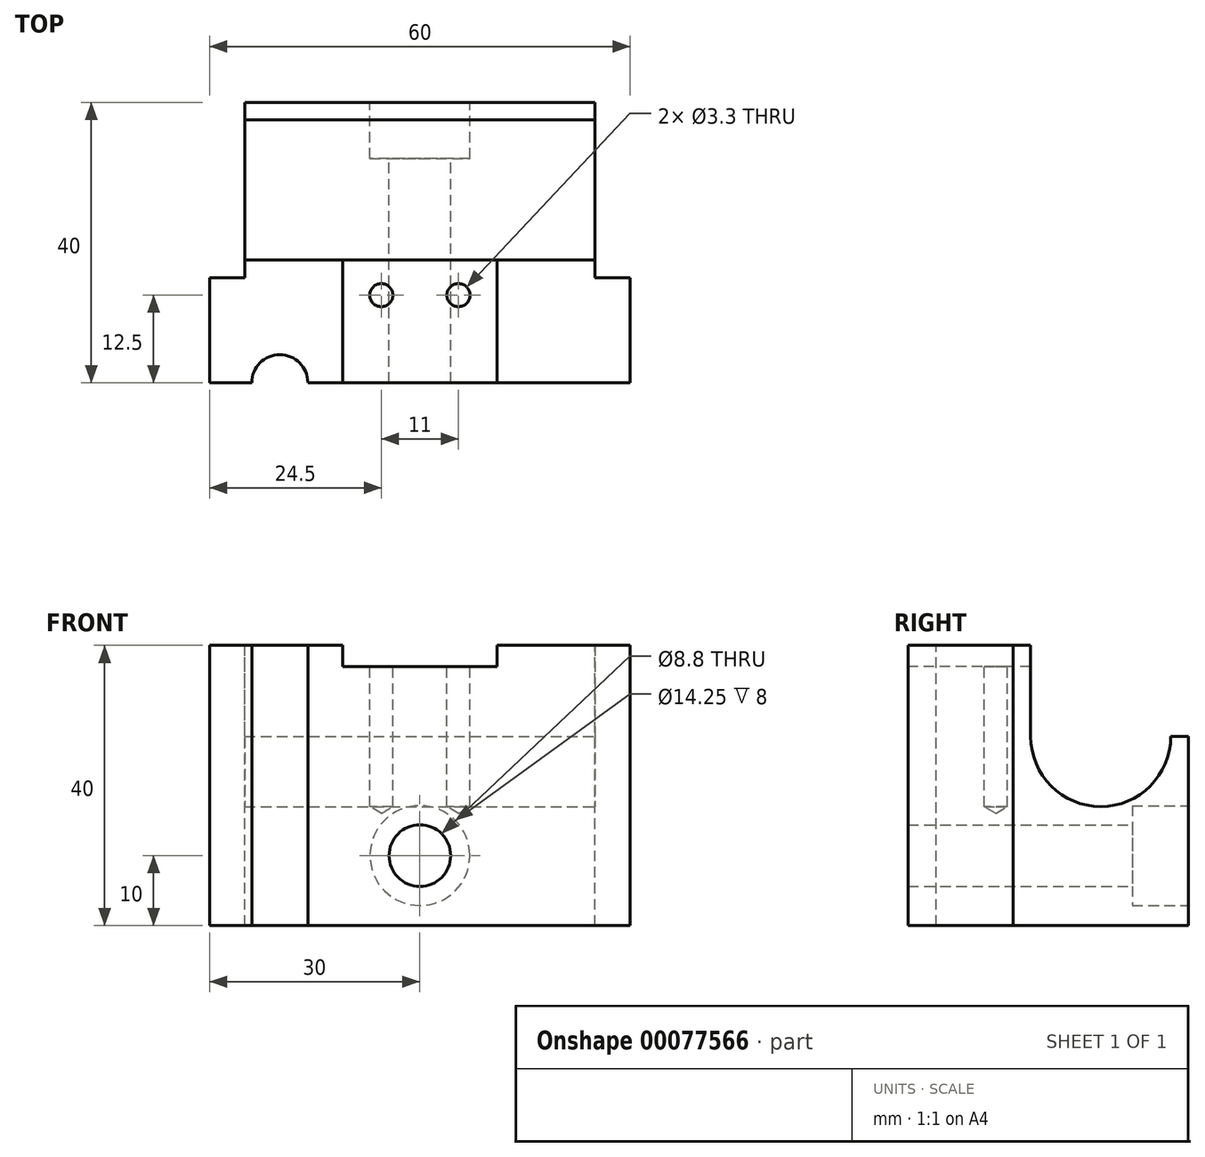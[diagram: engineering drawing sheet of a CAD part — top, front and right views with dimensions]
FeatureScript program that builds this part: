
annotation { "Feature Type Name" : "Feature", "Feature Type Description" : "" }
export const myFeature = defineFeature(function(context is Context, id is Id, definition is map)
    precondition{}
    {
        {
            var Q0;
            Q0=qCreatedBy(makeId("Top.planeOp"),FACE);
            var sketch = newSketch(context, id + "F0", { "sketchPlane" : qUnion([Q0])});
            skLineSegment(sketch, "E0.bottom", {"start": v(-30, 40) * mm, "end": v(30, 40) * mm});
            skLineSegment(sketch, "E0.top", {"start": v(-30, 0) * mm, "end": v(30, 0) * mm});
            skLineSegment(sketch, "E0.left", {"start": v(-30, 40) * mm, "end": v(-30, 0) * mm});
            skLineSegment(sketch, "E0.right", {"start": v(30, 40) * mm, "end": v(30, 0) * mm});
            skSolve(sketch);
        }
        {
            var Q0;
            Q0 = qSketchRegion(id + "F0", true);
            extrude(context, id + "F1", {"entities" : qUnion([Q0]), "depth" : 40 * mm});
        }
        {
            var Q0;
            Q0=makeQuery(id+"F1.opExtrude","CAP_FACE",FACE,{"disambiguationData":[OSD([sQuery(id+"F0.wireOp",EDGE,"E0.bottom"),sQuery(id+"F0.wireOp",EDGE,"E0.top"),sQuery(id+"F0.wireOp",EDGE,"E0.left"),sQuery(id+"F0.wireOp",EDGE,"E0.right")])],"isStart":false});
            var sketch = newSketch(context, id + "F2", { "sketchPlane" : qUnion([Q0])});
            skLineSegment(sketch, "E1.bottom", {"start": v(-30, 40) * mm, "end": v(-25, 40) * mm});
            skLineSegment(sketch, "E1.top", {"start": v(-30, 15) * mm, "end": v(-25, 15) * mm});
            skLineSegment(sketch, "E1.left", {"start": v(-30, 40) * mm, "end": v(-30, 15) * mm});
            skLineSegment(sketch, "E1.right", {"start": v(-25, 40) * mm, "end": v(-25, 15) * mm});
            skLineSegment(sketch, "E2.MirrorCS", {"start": v(30, 40) * mm, "end": v(25, 40) * mm});
            skLineSegment(sketch, "E3.MirrorCS", {"start": v(30, 15) * mm, "end": v(25, 15) * mm});
            skLineSegment(sketch, "E4.MirrorCS", {"start": v(30, 40) * mm, "end": v(30, 15) * mm});
            skLineSegment(sketch, "E5.MirrorCS", {"start": v(25, 40) * mm, "end": v(25, 15) * mm});
            skSolve(sketch);
        }
        {
            var Q0;
            Q0=makeQuery(id+"F2.imprint","IMPRINT",FACE,{"disambiguationData":[TD([[makeQuery(id+"F2.imprint","IMPRINT",EDGE,{"derivedFrom":sQuery(id+"F2.wireOp",EDGE,"E1.bottom")}),-1.0]])]});
            var Q1;
            Q1=makeQuery(id+"F2.imprint","IMPRINT",FACE,{"disambiguationData":[TD([[makeQuery(id+"F2.imprint","IMPRINT",EDGE,{"derivedFrom":sQuery(id+"F2.wireOp",EDGE,"E2.MirrorCS")}),-1.0]])]});
            extrude(context, id + "F3", {"entities" : qUnion([Q0, Q1]), "operationType" : NewBodyOperationType.REMOVE, "endBound" : BoundingType.THROUGH_ALL, "oppositeDirection" : true, "depth" : 25 * mm});
        }
        {
            var Q0;
            Q0=makeQuery(id+"F3.boolean.opBoolean","COPY",FACE,{"derivedFrom":makeQuery(id+"F3.opExtrude","SWEPT_FACE",FACE,{"disambiguationData":[OSD([sQuery(id+"F2.wireOp",EDGE,"E5.MirrorCS")])]})});
            var sketch = newSketch(context, id + "F4", { "sketchPlane" : qUnion([Q0])});
            skCircle(sketch, "E6", {"center": v(27.5, 27) * mm, "radius": 10 * mm});
            skLineSegment(sketch, "E7", {"start": v(17.5, 40) * mm, "end": v(17.5, 27) * mm});
            skLineSegment(sketch, "E8", {"start": v(40, 40) * mm, "end": v(40, 27) * mm});
            skLineSegment(sketch, "E9", {"start": v(37.5, 27) * mm, "end": v(40, 27) * mm});
            skLineSegment(sketch, "E10", {"start": v(17.5, 40) * mm, "end": v(40, 40) * mm});
            skSolve(sketch);
        }
        {
            var Q0;
            {var subQ0=sQuery(id+"F4.wireOp",EDGE,"E6");var subQ1=makeQuery(id+"F4.imprint","INTERSECT",VERTEX,{"derivedFrom":[subQ0,sQuery(id+"F4.wireOp",EDGE,"E7")]});Q0=makeQuery(id+"F4.imprint","IMPRINT",FACE,{"disambiguationData":[TD([[makeQuery(id+"F4.imprint","IMPRINT",EDGE,{"disambiguationData":[TD([[subQ1,1.0]])],"derivedFrom":subQ0}),1.0]])]});}
            var Q1;
            {var subQ1=sQuery(id+"F4.wireOp",EDGE,"E7");Q1=makeQuery(id+"F4.imprint","IMPRINT",FACE,{"disambiguationData":[TD([[makeQuery(id+"F4.imprint","IMPRINT",EDGE,{"derivedFrom":subQ1}),1.0]])]});}
            extrude(context, id + "F5", {"entities" : qUnion([Q0, Q1]), "operationType" : NewBodyOperationType.REMOVE, "endBound" : BoundingType.THROUGH_ALL, "oppositeDirection" : true, "depth" : 25 * mm});
        }
        {
            var Q0;
            Q0=makeQuery(id+"F1.opExtrude","CAP_FACE",FACE,{"disambiguationData":[OSD([sQuery(id+"F0.wireOp",EDGE,"E0.bottom"),sQuery(id+"F0.wireOp",EDGE,"E0.top"),sQuery(id+"F0.wireOp",EDGE,"E0.left"),sQuery(id+"F0.wireOp",EDGE,"E0.right")])],"isStart":false});
            var sketch = newSketch(context, id + "F6", { "sketchPlane" : qUnion([Q0])});
            skCircle(sketch, "E11", {"center": v(-20, 0) * mm, "radius": 4 * mm});
            skCircle(sketch, "E12.MirrorC", {"center": v(20, 0) * mm, "radius": 4 * mm});
            skSolve(sketch);
        }
        {
            var Q0;
            {var subQ0=sQuery(id+"F6.wireOp",EDGE,"E11");var subQ1=makeQuery(id+"F1.opExtrude","CAP_EDGE",EDGE,{"disambiguationData":[OSD([sQuery(id+"F0.wireOp",EDGE,"E0.top")])],"isStart":false});var subQ2=makeQuery(id+"F6.imprint","INTERSECT",VERTEX,{"disambiguationData":[OD(0.0)],"derivedFrom":[subQ1,subQ0]});Q0=makeQuery(id+"F6.imprint","IMPRINT",FACE,{"disambiguationData":[TD([[makeQuery(id+"F6.imprint","IMPRINT",EDGE,{"disambiguationData":[TD([[subQ2,1.0]])],"derivedFrom":subQ0}),1.0]])]});}
            var Q1;
            {var subQ0=sQuery(id+"F6.wireOp",EDGE,"E12.MirrorC");var subQ1=makeQuery(id+"F1.opExtrude","CAP_EDGE",EDGE,{"disambiguationData":[OSD([sQuery(id+"F0.wireOp",EDGE,"E0.top")])],"isStart":false});var subQ2=makeQuery(id+"F6.imprint","INTERSECT",VERTEX,{"disambiguationData":[OD(0.0)],"derivedFrom":[subQ1,subQ0]});Q1=makeQuery(id+"F6.imprint","IMPRINT",FACE,{"disambiguationData":[TD([[makeQuery(id+"F6.imprint","IMPRINT",EDGE,{"disambiguationData":[TD([[subQ2,1.0]])],"derivedFrom":subQ0}),-1.0]])]});}
            extrude(context, id + "F7", {"entities" : qUnion([Q0, Q1]), "operationType" : NewBodyOperationType.REMOVE, "endBound" : BoundingType.THROUGH_ALL, "oppositeDirection" : true, "depth" : 25 * mm});
        }
        {
            var Q0;
            Q0=makeQuery(id+"F1.opExtrude","CAP_FACE",FACE,{"disambiguationData":[OSD([sQuery(id+"F0.wireOp",EDGE,"E0.bottom"),sQuery(id+"F0.wireOp",EDGE,"E0.top"),sQuery(id+"F0.wireOp",EDGE,"E0.left"),sQuery(id+"F0.wireOp",EDGE,"E0.right")])],"isStart":false});
            var sketch = newSketch(context, id + "F8", { "sketchPlane" : qUnion([Q0])});
            skPoint(sketch, "E13.visualSharp", {"position": v(-22.75, -1.97) * mm});
            skPoint(sketch, "E14.visualSharp", {"position": v(20, -1.97) * mm});
            skLineSegment(sketch, "E15.bottom", {"start": v(-11, 17.5) * mm, "end": v(11, 17.5) * mm});
            skLineSegment(sketch, "E15.top", {"start": v(-11, 0) * mm, "end": v(11, 0) * mm});
            skLineSegment(sketch, "E15.left", {"start": v(-11, 17.5) * mm, "end": v(-11, 0) * mm});
            skLineSegment(sketch, "E15.right", {"start": v(11, 17.5) * mm, "end": v(11, 0) * mm});
            skSolve(sketch);
        }
        {
            var Q0;
            Q0=makeQuery(id+"F8.imprint","IMPRINT",FACE,{"disambiguationData":[TD([[makeQuery(id+"F8.imprint","IMPRINT",EDGE,{"derivedFrom":sQuery(id+"F8.wireOp",EDGE,"E15.bottom")}),-1.0]])]});
            extrude(context, id + "F9", {"entities" : qUnion([Q0]), "operationType" : NewBodyOperationType.REMOVE, "oppositeDirection" : true, "depth" : 3 * mm});
        }
        {
            var Q0;
            Q0=makeQuery(id+"F9.boolean.opBoolean","COPY",FACE,{"derivedFrom":makeQuery(id+"F9.opExtrude","CAP_FACE",FACE,{"disambiguationData":[OSD([sQuery(id+"F8.wireOp",EDGE,"E15.bottom"),sQuery(id+"F8.wireOp",EDGE,"E15.top"),sQuery(id+"F8.wireOp",EDGE,"E15.left"),sQuery(id+"F8.wireOp",EDGE,"E15.right")])],"isStart":false})});
            var sketch = newSketch(context, id + "F10", { "sketchPlane" : qUnion([Q0])});
            skPoint(sketch, "E16", {"position": v(-5.5, 12.5) * mm});
            skPoint(sketch, "E17.MirrorP", {"position": v(5.5, 12.5) * mm});
            skSolve(sketch);
        }
        {
            var Q0;
            Q0=sQuery(id+"F10.wireOp",VERTEX,"E16");
            var Q1;
            Q1=sQuery(id+"F10.wireOp",VERTEX,"E17.MirrorP");
            var Q2;
            Q2=makeQuery(id+"F1.opExtrude","SWEPT_BODY",BODY,{"disambiguationData":[OSD([sQuery(id+"F0.wireOp",EDGE,"E0.bottom"),sQuery(id+"F0.wireOp",EDGE,"E0.top"),sQuery(id+"F0.wireOp",EDGE,"E0.left"),sQuery(id+"F0.wireOp",EDGE,"E0.right")])]});
            hole(context, id + "F11", {"style" : HoleStyle.SIMPLE, "endStyle" : HoleEndStyle.BLIND, "standardTappedOrClearance" : lookupTablePath({ "standard" : "ISO", "fit" : "Normal", "size" : "M3", "type" : "Clearance" }), "standardBlindInLast" : lookupTablePath({ "fit" : "Standard", "standard" : "ISO", "size" : "M3", "type" : "Clearance" }), "holeDiameter" : 3.3 * mm, "holeDepth" : 20 * mm, "startFromSketch" : true, "locations" : qUnion([Q0, Q1]), "scope" : qUnion([Q2])});
        }
        {
            var Q0;
            Q0=makeQuery(id+"F1.opExtrude","SWEPT_FACE",FACE,{"disambiguationData":[OSD([sQuery(id+"F0.wireOp",EDGE,"E0.bottom")])]});
            var sketch = newSketch(context, id + "F12", { "sketchPlane" : qUnion([Q0])});
            skPoint(sketch, "E18", {"position": v(0, 10) * mm});
            skSolve(sketch);
        }
        {
            var Q0;
            Q0=sQuery(id+"F12.wireOp",VERTEX,"E18");
            var Q1;
            Q1=makeQuery(id+"F1.opExtrude","SWEPT_BODY",BODY,{"disambiguationData":[OSD([sQuery(id+"F0.wireOp",EDGE,"E0.bottom"),sQuery(id+"F0.wireOp",EDGE,"E0.top"),sQuery(id+"F0.wireOp",EDGE,"E0.left"),sQuery(id+"F0.wireOp",EDGE,"E0.right")])]});
            hole(context, id + "F13", {"style" : HoleStyle.C_BORE, "endStyle" : HoleEndStyle.BLIND, "standardTappedOrClearance" : lookupTablePath({ "standard" : "ISO", "fit" : "Normal", "size" : "M8", "type" : "Clearance" }), "standardBlindInLast" : lookupTablePath({ "fit" : "Standard", "standard" : "ISO", "size" : "M8", "type" : "Clearance" }), "holeDiameter" : 8.8 * mm, "cBoreDiameter" : 14.25 * mm, "cBoreDepth" : 8 * mm, "holeDepth" : 50 * mm, "startFromSketch" : true, "locations" : qUnion([Q0]), "scope" : qUnion([Q1])});
        }
    });
